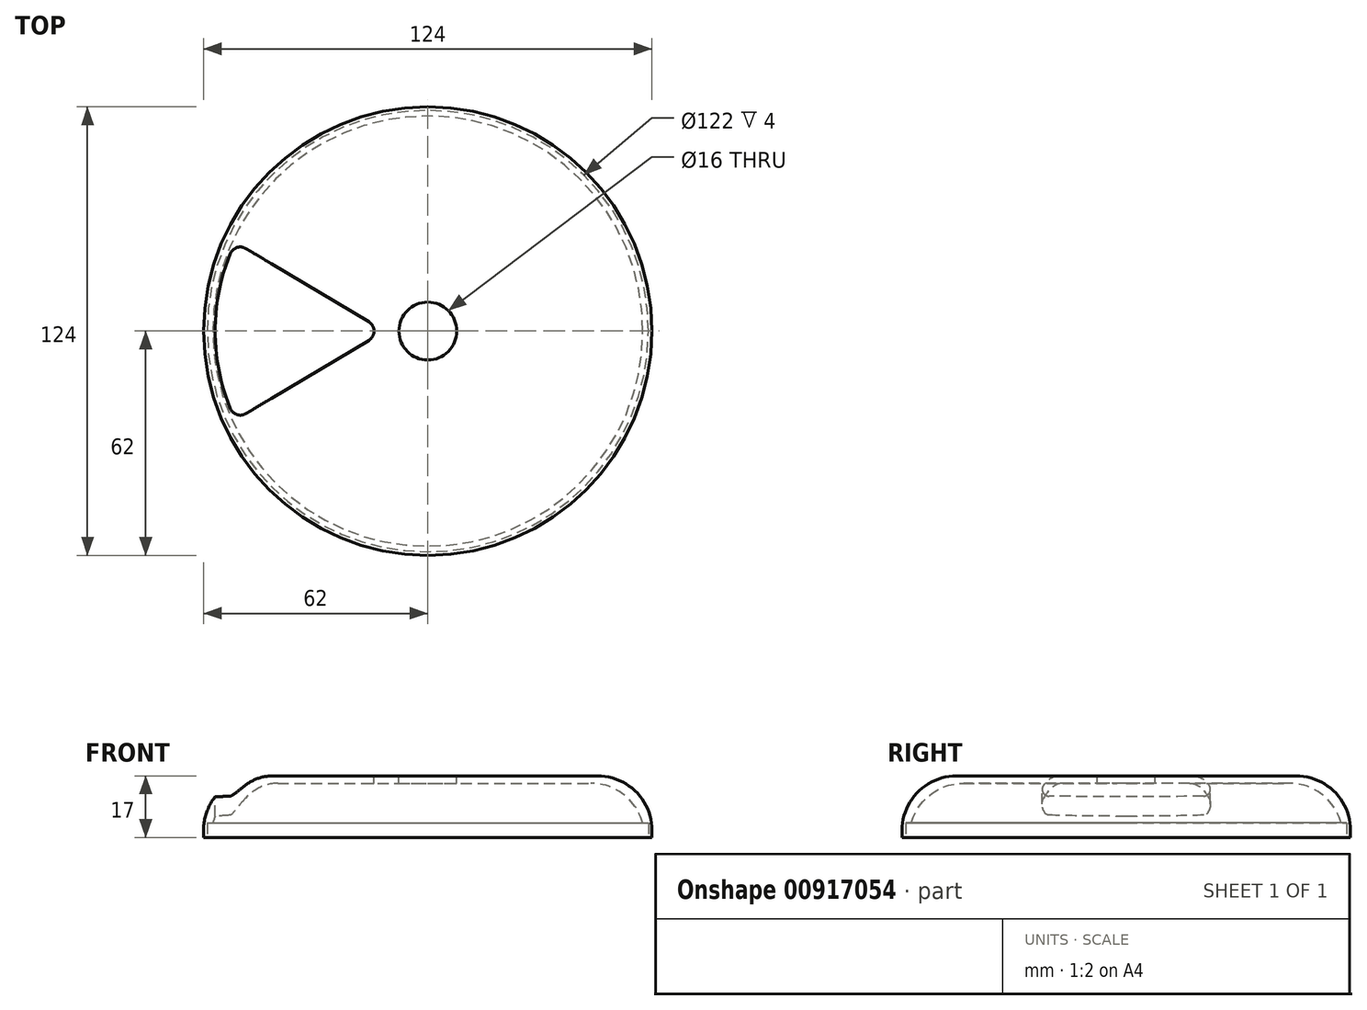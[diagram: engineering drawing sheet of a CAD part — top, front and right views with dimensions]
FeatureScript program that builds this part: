
annotation { "Feature Type Name" : "Feature", "Feature Type Description" : "" }
export const myFeature = defineFeature(function(context is Context, id is Id, definition is map)
    precondition{}
    {
        {
            var Q0;
            Q0=qCreatedBy(makeId("Top.planeOp"),FACE);
            var sketch = newSketch(context, id + "F0", { "sketchPlane" : qUnion([Q0])});
            skCircle(sketch, "E0", {"center": v(0, 0) * mm, "radius": 62 * mm});
            skSolve(sketch);
        }
        {
            var Q0;
            Q0=makeQuery(id+"F0.imprint","IMPRINT",FACE,{"disambiguationData":[TD([[makeQuery(id+"F0.imprint","IMPRINT",EDGE,{"derivedFrom":sQuery(id+"F0.wireOp",EDGE,"E0")}),1.0]])]});
            extrude(context, id + "F1", {"entities" : qUnion([Q0]), "depth" : 17 * mm, "offsetDistance" : 25 * mm});
        }
        {
            var Q0;
            Q0=makeQuery(id+"F1.opExtrude","CAP_FACE",FACE,{"disambiguationData":[OSD([sQuery(id+"F0.wireOp",EDGE,"E0")])],"isStart":true});
            var sketch = newSketch(context, id + "F2", { "sketchPlane" : qUnion([Q0])});
            skCircle(sketch, "E1", {"center": v(0, 0) * mm, "radius": 60 * mm});
            skSolve(sketch);
        }
        {
            var Q0;
            Q0=makeQuery(id+"F2.imprint","IMPRINT",FACE,{"disambiguationData":[TD([[makeQuery(id+"F2.imprint","IMPRINT",EDGE,{"derivedFrom":sQuery(id+"F2.wireOp",EDGE,"E1")}),1.0]])]});
            extrude(context, id + "F3", {"entities" : qUnion([Q0]), "operationType" : NewBodyOperationType.REMOVE, "oppositeDirection" : true, "depth" : 15 * mm, "offsetDistance" : 25 * mm});
        }
        {
            var Q0;
            Q0=makeQuery(id+"F3.boolean.opBoolean","COPY",EDGE,{"derivedFrom":makeQuery(id+"F3.opExtrude","CAP_EDGE",EDGE,{"disambiguationData":[OSD([sQuery(id+"F2.wireOp",EDGE,"E1")])],"isStart":false})});
            var Q1;
            Q1=makeQuery(id+"F1.opExtrude","CAP_EDGE",EDGE,{"disambiguationData":[OSD([sQuery(id+"F0.wireOp",EDGE,"E0")])],"isStart":false});
            fillet(context, id + "F4", {"entities" : qUnion([Q0, Q1]), "radius" : 15 * mm, "tangentPropagation" : true, "allowEdgeOverflow" : false});
        }
        {
            var Q0;
            Q0=makeQuery(id+"F1.opExtrude","CAP_FACE",FACE,{"disambiguationData":[OSD([sQuery(id+"F0.wireOp",EDGE,"E0")])],"isStart":true});
            var sketch = newSketch(context, id + "F5", { "sketchPlane" : qUnion([Q0])});
            skCircle(sketch, "E2", {"center": v(0, 0) * mm, "radius": 61 * mm});
            skSolve(sketch);
        }
        {
            var Q0;
            Q0 = qSketchRegion(id + "F5", true);
            extrude(context, id + "F6", {"entities" : qUnion([Q0]), "operationType" : NewBodyOperationType.REMOVE, "oppositeDirection" : true, "depth" : 4 * mm, "offsetDistance" : 25 * mm});
        }
        {
            var Q0;
            Q0=makeQuery(id+"F1.opExtrude","CAP_FACE",FACE,{"disambiguationData":[OSD([sQuery(id+"F0.wireOp",EDGE,"E0")])],"isStart":false});
            var sketch = newSketch(context, id + "F7", { "sketchPlane" : qUnion([Q0])});
            skPoint(sketch, "E3", {"position": v(47, 0) * mm});
            skPoint(sketch, "E4.1.0", {"position": v(29.3, 36.75) * mm});
            skPoint(sketch, "E4.2.0", {"position": v(-10.46, 45.82) * mm});
            skPoint(sketch, "E4.3.0", {"position": v(-42.35, 20.4) * mm});
            skPoint(sketch, "E4.4.0", {"position": v(-42.35, -20.4) * mm});
            skPoint(sketch, "E4.5.0", {"position": v(-10.46, -45.82) * mm});
            skPoint(sketch, "E4.6.0", {"position": v(29.3, -36.75) * mm});
            skPoint(sketch, "E4.center", {"position": v(0, 0) * mm});
            skPoint(sketch, "E5", {"position": v(-43.17, 18.57) * mm});
            skPoint(sketch, "E6", {"position": v(-43.17, -18.57) * mm});
            skPoint(sketch, "E7", {"position": v(-12, 0) * mm});
            skLineSegment(sketch, "E8", {"start": v(-12, 0) * mm, "end": v(-53.24, 24.57) * mm});
            skLineSegment(sketch, "E9", {"start": v(-12, 0) * mm, "end": v(-53.24, -24.57) * mm});
            skArc(sketch, "E10", {"start": v(-53.24, 24.57) * mm, "mid": v(-58.8, 0) * mm, "end": v(-53.24, -24.57) * mm});
            skSolve(sketch);
        }
        {
            var Q0;
            {var subQ0=sQuery(id+"F7.wireOp",EDGE,"E9");var subQ1=sQuery(id+"F7.wireOp",EDGE,"E8");var subQ2=makeQuery(id+"F7.imprint","INTERSECT",VERTEX,{"derivedFrom":[subQ1,subQ0]});Q0=makeQuery(id+"F7.imprint","IMPRINT",FACE,{"disambiguationData":[TD([[makeQuery(id+"F7.imprint","IMPRINT",EDGE,{"disambiguationData":[TD([[subQ2,-1.0]])],"derivedFrom":subQ1}),1.0]])]});}
            var Q1;
            {var subQ0=sQuery(id+"F7.wireOp",EDGE,"E10");Q1=makeQuery(id+"F7.imprint","IMPRINT",FACE,{"disambiguationData":[TD([[makeQuery(id+"F7.imprint","IMPRINT",EDGE,{"derivedFrom":subQ0}),1.0]])]});}
            extrude(context, id + "F8", {"entities" : qUnion([Q0, Q1]), "operationType" : NewBodyOperationType.REMOVE, "oppositeDirection" : true, "depth" : 25 * mm, "offsetDistance" : 25 * mm});
        }
        {
            var Q0;
            Q0=makeQuery(id+"F8.boolean.opBoolean","COPY",EDGE,{"derivedFrom":makeQuery(id+"F8.opExtrude","SWEPT_EDGE",EDGE,{"disambiguationData":[OSD([sQuery(id+"F7.wireOp",EDGE,"E8"),sQuery(id+"F7.wireOp",EDGE,"E9")])]})});
            var Q1;
            Q1=makeQuery(id+"F8.boolean.opBoolean","COPY",EDGE,{"derivedFrom":makeQuery(id+"F8.opExtrude","SWEPT_EDGE",EDGE,{"disambiguationData":[OSD([sQuery(id+"F7.wireOp",EDGE,"E9"),sQuery(id+"F7.wireOp",EDGE,"E10")])]})});
            var Q2;
            Q2=makeQuery(id+"F8.boolean.opBoolean","COPY",EDGE,{"derivedFrom":makeQuery(id+"F8.opExtrude","SWEPT_EDGE",EDGE,{"disambiguationData":[OSD([sQuery(id+"F7.wireOp",EDGE,"E8"),sQuery(id+"F7.wireOp",EDGE,"E10")])]})});
            fillet(context, id + "F9", {"entities" : qUnion([Q0, Q1, Q2]), "radius" : 3 * mm, "tangentPropagation" : true, "allowEdgeOverflow" : false});
        }
        {
            var Q0;
            Q0=makeQuery(id+"F1.opExtrude","CAP_FACE",FACE,{"disambiguationData":[OSD([sQuery(id+"F0.wireOp",EDGE,"E0")])],"isStart":false});
            var sketch = newSketch(context, id + "F10", { "sketchPlane" : qUnion([Q0])});
            skCircle(sketch, "E11", {"center": v(0, 0) * mm, "radius": 8 * mm});
            skSolve(sketch);
        }
        {
            var Q0;
            Q0=makeQuery(id+"F10.imprint","IMPRINT",FACE,{"disambiguationData":[TD([[makeQuery(id+"F10.imprint","IMPRINT",EDGE,{"derivedFrom":sQuery(id+"F10.wireOp",EDGE,"E11")}),1.0]])]});
            extrude(context, id + "F11", {"entities" : qUnion([Q0]), "operationType" : NewBodyOperationType.REMOVE, "oppositeDirection" : true, "depth" : 25 * mm, "offsetDistance" : 25 * mm});
        }
    });
